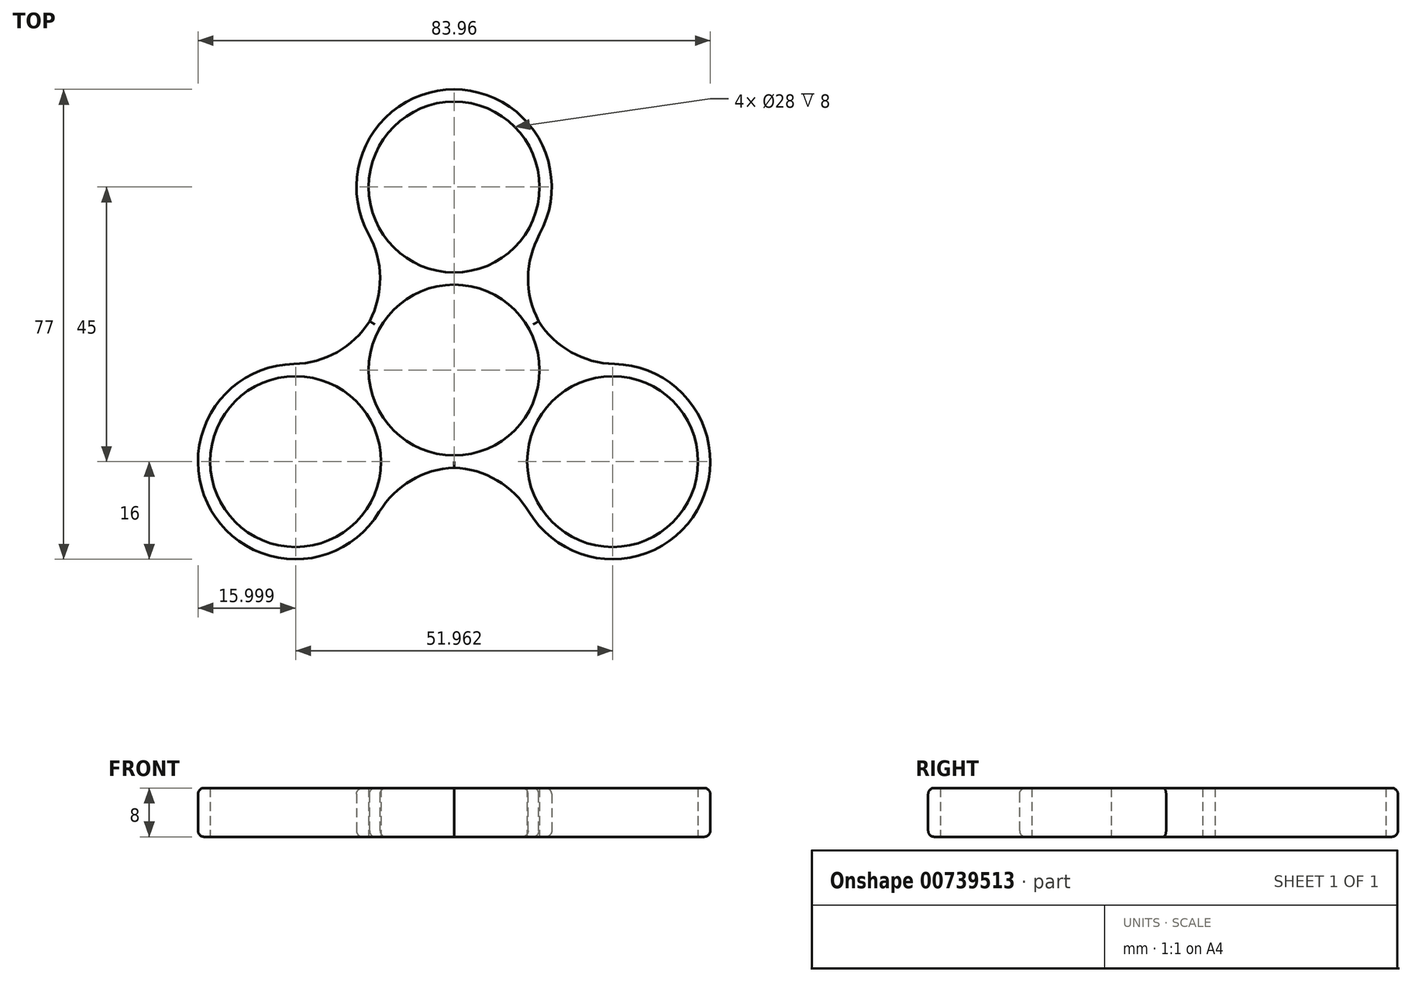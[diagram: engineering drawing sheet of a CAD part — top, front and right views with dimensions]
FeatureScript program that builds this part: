
annotation { "Feature Type Name" : "Feature", "Feature Type Description" : "" }
export const myFeature = defineFeature(function(context is Context, id is Id, definition is map)
    precondition{}
    {
        {
            var Q0;
            Q0=qCreatedBy(makeId("Top.planeOp"),FACE);
            var sketch = newSketch(context, id + "F0", { "sketchPlane" : qUnion([Q0])});
            skCircle(sketch, "E0", {"center": v(0, 0) * mm, "radius": 14 * mm});
            skCircle(sketch, "E1", {"center": v(25.98, -15) * mm, "radius": 14 * mm});
            skCircle(sketch, "E2", {"center": v(-25.98, -15) * mm, "radius": 14 * mm});
            skCircle(sketch, "E3", {"center": v(0, 30) * mm, "radius": 14 * mm});
            skCircle(sketch, "E4", {"center": v(0, 0) * mm, "radius": 30 * mm});
            skLineSegment(sketch, "E5", {"start": v(0, 0) * mm, "end": v(0, 45.5) * mm});
            skLineSegment(sketch, "E6", {"start": v(0, 0) * mm, "end": v(46, -26.56) * mm});
            skLineSegment(sketch, "E7", {"start": v(0, 0) * mm, "end": v(-45.6, -26.33) * mm});
            skCircle(sketch, "E8", {"center": v(0, 30) * mm, "radius": 16 * mm});
            skCircle(sketch, "E9", {"center": v(0, 0) * mm, "radius": 16 * mm});
            skCircle(sketch, "E10", {"center": v(-25.98, -15) * mm, "radius": 16 * mm});
            skCircle(sketch, "E11", {"center": v(25.98, -15) * mm, "radius": 16 * mm});
            skSolve(sketch);
        }
        {
            var Q0;
            {var subQ0=sQuery(id+"F0.wireOp",EDGE,"E4");var subQ1=sQuery(id+"F0.wireOp",EDGE,"E1");var subQ2=makeQuery(id+"F0.imprint","INTERSECT",VERTEX,{"disambiguationData":[OD(1.0)],"derivedFrom":[subQ1,subQ0]});Q0=makeQuery(id+"F0.imprint","IMPRINT",FACE,{"disambiguationData":[TD([[makeQuery(id+"F0.imprint","IMPRINT",EDGE,{"disambiguationData":[TD([[subQ2,-1.0]])],"derivedFrom":subQ1}),-1.0]])]});}
            var Q1;
            {var subQ0=sQuery(id+"F0.wireOp",EDGE,"E4");var subQ1=sQuery(id+"F0.wireOp",EDGE,"E1");var subQ2=makeQuery(id+"F0.imprint","INTERSECT",VERTEX,{"disambiguationData":[OD(0.0)],"derivedFrom":[subQ1,subQ0]});Q1=makeQuery(id+"F0.imprint","IMPRINT",FACE,{"disambiguationData":[TD([[makeQuery(id+"F0.imprint","IMPRINT",EDGE,{"disambiguationData":[TD([[subQ2,1.0]])],"derivedFrom":subQ1}),-1.0]])]});}
            var Q2;
            {var subQ0=sQuery(id+"F0.wireOp",EDGE,"E4");var subQ1=sQuery(id+"F0.wireOp",EDGE,"E2");var subQ2=makeQuery(id+"F0.imprint","INTERSECT",VERTEX,{"disambiguationData":[OD(0.0)],"derivedFrom":[subQ1,subQ0]});Q2=makeQuery(id+"F0.imprint","IMPRINT",FACE,{"disambiguationData":[TD([[makeQuery(id+"F0.imprint","IMPRINT",EDGE,{"disambiguationData":[TD([[subQ2,-1.0]])],"derivedFrom":subQ1}),-1.0]])]});}
            var Q3;
            {var subQ0=sQuery(id+"F0.wireOp",EDGE,"E7");var subQ1=sQuery(id+"F0.wireOp",EDGE,"E2");var subQ2=makeQuery(id+"F0.imprint","INTERSECT",VERTEX,{"derivedFrom":[subQ1,subQ0]});Q3=makeQuery(id+"F0.imprint","IMPRINT",FACE,{"disambiguationData":[TD([[makeQuery(id+"F0.imprint","IMPRINT",EDGE,{"disambiguationData":[TD([[subQ2,-1.0]])],"derivedFrom":subQ1}),-1.0]])]});}
            var Q4;
            {var subQ0=sQuery(id+"F0.wireOp",EDGE,"E4");var subQ5=sQuery(id+"F0.wireOp",EDGE,"E11");var subQ6=makeQuery(id+"F0.imprint","INTERSECT",VERTEX,{"disambiguationData":[OD(0.0)],"derivedFrom":[subQ0,subQ5]});Q4=makeQuery(id+"F0.imprint","IMPRINT",FACE,{"disambiguationData":[TD([[makeQuery(id+"F0.imprint","IMPRINT",EDGE,{"disambiguationData":[TD([[subQ6,1.0]])],"derivedFrom":subQ0}),1.0]])]});}
            var Q5;
            {var subQ0=sQuery(id+"F0.wireOp",EDGE,"E4");var subQ5=sQuery(id+"F0.wireOp",EDGE,"E11");var subQ6=makeQuery(id+"F0.imprint","INTERSECT",VERTEX,{"disambiguationData":[OD(1.0)],"derivedFrom":[subQ0,subQ5]});Q5=makeQuery(id+"F0.imprint","IMPRINT",FACE,{"disambiguationData":[TD([[makeQuery(id+"F0.imprint","IMPRINT",EDGE,{"disambiguationData":[TD([[subQ6,-1.0]])],"derivedFrom":subQ0}),1.0]])]});}
            var Q6;
            {var subQ0=sQuery(id+"F0.wireOp",EDGE,"E4");var subQ5=sQuery(id+"F0.wireOp",EDGE,"E10");var subQ7=makeQuery(id+"F0.imprint","INTERSECT",VERTEX,{"disambiguationData":[OD(0.0)],"derivedFrom":[subQ0,subQ5]});Q6=makeQuery(id+"F0.imprint","IMPRINT",FACE,{"disambiguationData":[TD([[makeQuery(id+"F0.imprint","IMPRINT",EDGE,{"disambiguationData":[TD([[subQ7,-1.0]])],"derivedFrom":subQ0}),1.0]])]});}
            var Q7;
            {var subQ0=sQuery(id+"F0.wireOp",EDGE,"E4");var subQ5=sQuery(id+"F0.wireOp",EDGE,"E10");var subQ6=makeQuery(id+"F0.imprint","INTERSECT",VERTEX,{"disambiguationData":[OD(1.0)],"derivedFrom":[subQ0,subQ5]});Q7=makeQuery(id+"F0.imprint","IMPRINT",FACE,{"disambiguationData":[TD([[makeQuery(id+"F0.imprint","IMPRINT",EDGE,{"disambiguationData":[TD([[subQ6,1.0]])],"derivedFrom":subQ0}),1.0]])]});}
            var Q8;
            {var subQ3=sQuery(id+"F0.wireOp",EDGE,"E3");var subQ5=makeQuery(id+"F0.imprint","INTERSECT",VERTEX,{"derivedFrom":[subQ3,sQuery(id+"F0.wireOp",EDGE,"E5")]});Q8=makeQuery(id+"F0.imprint","IMPRINT",FACE,{"disambiguationData":[TD([[makeQuery(id+"F0.imprint","IMPRINT",EDGE,{"disambiguationData":[TD([[subQ5,-1.0]])],"derivedFrom":subQ3}),-1.0]])]});}
            var Q9;
            {var subQ0=sQuery(id+"F0.wireOp",EDGE,"E4");var subQ5=sQuery(id+"F0.wireOp",EDGE,"E8");var subQ6=makeQuery(id+"F0.imprint","INTERSECT",VERTEX,{"disambiguationData":[OD(1.0)],"derivedFrom":[subQ0,subQ5]});Q9=makeQuery(id+"F0.imprint","IMPRINT",FACE,{"disambiguationData":[TD([[makeQuery(id+"F0.imprint","IMPRINT",EDGE,{"disambiguationData":[TD([[subQ6,1.0]])],"derivedFrom":subQ0}),1.0]])]});}
            var Q10;
            {var subQ0=sQuery(id+"F0.wireOp",EDGE,"E4");var subQ5=sQuery(id+"F0.wireOp",EDGE,"E8");var subQ6=makeQuery(id+"F0.imprint","INTERSECT",VERTEX,{"disambiguationData":[OD(0.0)],"derivedFrom":[subQ0,subQ5]});Q10=makeQuery(id+"F0.imprint","IMPRINT",FACE,{"disambiguationData":[TD([[makeQuery(id+"F0.imprint","IMPRINT",EDGE,{"disambiguationData":[TD([[subQ6,-1.0]])],"derivedFrom":subQ0}),1.0]])]});}
            var Q11;
            {var subQ0=sQuery(id+"F0.wireOp",EDGE,"E10");var subQ5=sQuery(id+"F0.wireOp",EDGE,"E9");var subQ7=makeQuery(id+"F0.imprint","INTERSECT",VERTEX,{"disambiguationData":[OD(1.0)],"derivedFrom":[subQ5,subQ0]});Q11=makeQuery(id+"F0.imprint","IMPRINT",FACE,{"disambiguationData":[TD([[makeQuery(id+"F0.imprint","IMPRINT",EDGE,{"disambiguationData":[TD([[subQ7,-1.0]])],"derivedFrom":subQ5}),1.0]])]});}
            var Q12;
            {var subQ3=sQuery(id+"F0.wireOp",EDGE,"E8");var subQ5=sQuery(id+"F0.wireOp",EDGE,"E9");var subQ6=makeQuery(id+"F0.imprint","INTERSECT",VERTEX,{"disambiguationData":[OD(0.0)],"derivedFrom":[subQ3,subQ5]});Q12=makeQuery(id+"F0.imprint","IMPRINT",FACE,{"disambiguationData":[TD([[makeQuery(id+"F0.imprint","IMPRINT",EDGE,{"disambiguationData":[TD([[subQ6,-1.0]])],"derivedFrom":subQ5}),1.0]])]});}
            var Q13;
            {var subQ0=sQuery(id+"F0.wireOp",EDGE,"E10");var subQ3=sQuery(id+"F0.wireOp",EDGE,"E9");var subQ5=makeQuery(id+"F0.imprint","INTERSECT",VERTEX,{"disambiguationData":[OD(0.0)],"derivedFrom":[subQ3,subQ0]});Q13=makeQuery(id+"F0.imprint","IMPRINT",FACE,{"disambiguationData":[TD([[makeQuery(id+"F0.imprint","IMPRINT",EDGE,{"disambiguationData":[TD([[subQ5,-1.0]])],"derivedFrom":subQ3}),1.0]])]});}
            var Q14;
            {var subQ0=sQuery(id+"F0.wireOp",EDGE,"E10");var subQ3=sQuery(id+"F0.wireOp",EDGE,"E9");var subQ5=makeQuery(id+"F0.imprint","INTERSECT",VERTEX,{"disambiguationData":[OD(1.0)],"derivedFrom":[subQ3,subQ0]});Q14=makeQuery(id+"F0.imprint","IMPRINT",FACE,{"disambiguationData":[TD([[makeQuery(id+"F0.imprint","IMPRINT",EDGE,{"disambiguationData":[TD([[subQ5,1.0]])],"derivedFrom":subQ3}),1.0]])]});}
            var Q15;
            {var subQ0=sQuery(id+"F0.wireOp",EDGE,"E11");var subQ3=sQuery(id+"F0.wireOp",EDGE,"E9");var subQ5=makeQuery(id+"F0.imprint","INTERSECT",VERTEX,{"disambiguationData":[OD(0.0)],"derivedFrom":[subQ3,subQ0]});Q15=makeQuery(id+"F0.imprint","IMPRINT",FACE,{"disambiguationData":[TD([[makeQuery(id+"F0.imprint","IMPRINT",EDGE,{"disambiguationData":[TD([[subQ5,-1.0]])],"derivedFrom":subQ3}),1.0]])]});}
            var Q16;
            {var subQ0=sQuery(id+"F0.wireOp",EDGE,"E11");var subQ3=sQuery(id+"F0.wireOp",EDGE,"E9");var subQ5=makeQuery(id+"F0.imprint","INTERSECT",VERTEX,{"disambiguationData":[OD(1.0)],"derivedFrom":[subQ3,subQ0]});Q16=makeQuery(id+"F0.imprint","IMPRINT",FACE,{"disambiguationData":[TD([[makeQuery(id+"F0.imprint","IMPRINT",EDGE,{"disambiguationData":[TD([[subQ5,1.0]])],"derivedFrom":subQ3}),1.0]])]});}
            var Q17;
            {var subQ0=sQuery(id+"F0.wireOp",EDGE,"E8");var subQ5=sQuery(id+"F0.wireOp",EDGE,"E9");var subQ6=makeQuery(id+"F0.imprint","INTERSECT",VERTEX,{"disambiguationData":[OD(1.0)],"derivedFrom":[subQ0,subQ5]});Q17=makeQuery(id+"F0.imprint","IMPRINT",FACE,{"disambiguationData":[TD([[makeQuery(id+"F0.imprint","IMPRINT",EDGE,{"disambiguationData":[TD([[subQ6,1.0]])],"derivedFrom":subQ5}),1.0]])]});}
            var Q18;
            {var subQ0=sQuery(id+"F0.wireOp",EDGE,"E8");var subQ3=sQuery(id+"F0.wireOp",EDGE,"E9");var subQ5=makeQuery(id+"F0.imprint","INTERSECT",VERTEX,{"disambiguationData":[OD(1.0)],"derivedFrom":[subQ0,subQ3]});Q18=makeQuery(id+"F0.imprint","IMPRINT",FACE,{"disambiguationData":[TD([[makeQuery(id+"F0.imprint","IMPRINT",EDGE,{"disambiguationData":[TD([[subQ5,1.0]])],"derivedFrom":subQ0}),1.0]])]});}
            var Q19;
            {var subQ0=sQuery(id+"F0.wireOp",EDGE,"E8");var subQ3=sQuery(id+"F0.wireOp",EDGE,"E9");var subQ5=makeQuery(id+"F0.imprint","INTERSECT",VERTEX,{"disambiguationData":[OD(0.0)],"derivedFrom":[subQ0,subQ3]});Q19=makeQuery(id+"F0.imprint","IMPRINT",FACE,{"disambiguationData":[TD([[makeQuery(id+"F0.imprint","IMPRINT",EDGE,{"disambiguationData":[TD([[subQ5,-1.0]])],"derivedFrom":subQ0}),1.0]])]});}
            extrude(context, id + "F1", {"entities" : qUnion([Q0, Q1, Q2, Q3, Q4, Q5, Q6, Q7, Q8, Q9, Q10, Q11, Q12, Q13, Q14, Q15, Q16, Q17, Q18, Q19]), "depth" : 8 * mm, "offsetDistance" : 25 * mm});
        }
        {
            var Q0;
            {var subQ0=sQuery(id+"F0.wireOp",EDGE,"E10");var subQ1=sQuery(id+"F0.wireOp",EDGE,"E9");Q0=makeQuery(id+"F1.opExtrude","SWEPT_EDGE",EDGE,{"disambiguationData":[OSD([subQ1,subQ0]),TDD([makeQuery(id+"F0.imprint","INTERSECT",VERTEX,{"disambiguationData":[OD(1.0)],"derivedFrom":[subQ1,subQ0]})])]});}
            var Q1;
            {var subQ0=sQuery(id+"F0.wireOp",EDGE,"E11");var subQ1=sQuery(id+"F0.wireOp",EDGE,"E9");Q1=makeQuery(id+"F1.opExtrude","SWEPT_EDGE",EDGE,{"disambiguationData":[OSD([subQ1,subQ0]),TDD([makeQuery(id+"F0.imprint","INTERSECT",VERTEX,{"disambiguationData":[OD(0.0)],"derivedFrom":[subQ1,subQ0]})])]});}
            var Q2;
            {var subQ0=sQuery(id+"F0.wireOp",EDGE,"E11");var subQ1=sQuery(id+"F0.wireOp",EDGE,"E9");Q2=makeQuery(id+"F1.opExtrude","SWEPT_EDGE",EDGE,{"disambiguationData":[OSD([subQ1,subQ0]),TDD([makeQuery(id+"F0.imprint","INTERSECT",VERTEX,{"disambiguationData":[OD(1.0)],"derivedFrom":[subQ1,subQ0]})])]});}
            var Q3;
            {var subQ0=sQuery(id+"F0.wireOp",EDGE,"E9");var subQ1=sQuery(id+"F0.wireOp",EDGE,"E8");Q3=makeQuery(id+"F1.opExtrude","SWEPT_EDGE",EDGE,{"disambiguationData":[OSD([subQ1,subQ0]),TDD([makeQuery(id+"F0.imprint","INTERSECT",VERTEX,{"disambiguationData":[OD(1.0)],"derivedFrom":[subQ1,subQ0]})])]});}
            var Q4;
            {var subQ0=sQuery(id+"F0.wireOp",EDGE,"E9");var subQ1=sQuery(id+"F0.wireOp",EDGE,"E8");Q4=makeQuery(id+"F1.opExtrude","SWEPT_EDGE",EDGE,{"disambiguationData":[OSD([subQ1,subQ0]),TDD([makeQuery(id+"F0.imprint","INTERSECT",VERTEX,{"disambiguationData":[OD(0.0)],"derivedFrom":[subQ1,subQ0]})])]});}
            var Q5;
            {var subQ0=sQuery(id+"F0.wireOp",EDGE,"E10");var subQ1=sQuery(id+"F0.wireOp",EDGE,"E9");Q5=makeQuery(id+"F1.opExtrude","SWEPT_EDGE",EDGE,{"disambiguationData":[OSD([subQ1,subQ0]),TDD([makeQuery(id+"F0.imprint","INTERSECT",VERTEX,{"disambiguationData":[OD(0.0)],"derivedFrom":[subQ1,subQ0]})])]});}
            fillet(context, id + "F2", {"entities" : qUnion([Q0, Q1, Q2, Q3, Q4, Q5]), "radius" : 15 * mm, "tangentPropagation" : true, "allowEdgeOverflow" : false});
        }
        {
            var Q0;
            Q0=makeQuery(id+"F1.opExtrude","CAP_EDGE",EDGE,{"disambiguationData":[OSD([sQuery(id+"F0.wireOp",EDGE,"E10")])],"isStart":false});
            var Q1;
            {var subQ0=sQuery(id+"F0.wireOp",EDGE,"E10");var subQ1=sQuery(id+"F0.wireOp",EDGE,"E9");Q1=makeQuery(id+"F2.opFillet","BLEND_EDGE",EDGE,{"blendedFrom":[makeQuery(id+"F1.opExtrude","SWEPT_EDGE",EDGE,{"disambiguationData":[OSD([subQ1,subQ0]),TDD([makeQuery(id+"F0.imprint","INTERSECT",VERTEX,{"disambiguationData":[OD(1.0)],"derivedFrom":[subQ1,subQ0]})])]}),makeQuery(id+"F1.opExtrude","CAP_FACE",FACE,{"disambiguationData":[OSD([sQuery(id+"F0.wireOp",EDGE,"E0"),sQuery(id+"F0.wireOp",EDGE,"E1"),sQuery(id+"F0.wireOp",EDGE,"E2"),sQuery(id+"F0.wireOp",EDGE,"E3"),sQuery(id+"F0.wireOp",EDGE,"E8"),subQ1,subQ0,sQuery(id+"F0.wireOp",EDGE,"E11")])],"isStart":false})],"blendedInto":[makeQuery(id+"F1.opExtrude","CAP_FACE",FACE,{"disambiguationData":[OSD([sQuery(id+"F0.wireOp",EDGE,"E0"),sQuery(id+"F0.wireOp",EDGE,"E1"),sQuery(id+"F0.wireOp",EDGE,"E2"),sQuery(id+"F0.wireOp",EDGE,"E3"),sQuery(id+"F0.wireOp",EDGE,"E8"),subQ1,subQ0,sQuery(id+"F0.wireOp",EDGE,"E11")])],"isStart":false})]});}
            var Q2;
            {var subQ0=sQuery(id+"F0.wireOp",EDGE,"E11");var subQ1=sQuery(id+"F0.wireOp",EDGE,"E9");Q2=makeQuery(id+"F2.opFillet","BLEND_EDGE",EDGE,{"blendedFrom":[makeQuery(id+"F1.opExtrude","SWEPT_EDGE",EDGE,{"disambiguationData":[OSD([subQ1,subQ0]),TDD([makeQuery(id+"F0.imprint","INTERSECT",VERTEX,{"disambiguationData":[OD(0.0)],"derivedFrom":[subQ1,subQ0]})])]}),makeQuery(id+"F1.opExtrude","CAP_FACE",FACE,{"disambiguationData":[OSD([sQuery(id+"F0.wireOp",EDGE,"E0"),sQuery(id+"F0.wireOp",EDGE,"E1"),sQuery(id+"F0.wireOp",EDGE,"E2"),sQuery(id+"F0.wireOp",EDGE,"E3"),sQuery(id+"F0.wireOp",EDGE,"E8"),subQ1,sQuery(id+"F0.wireOp",EDGE,"E10"),subQ0])],"isStart":false})],"blendedInto":[makeQuery(id+"F1.opExtrude","CAP_FACE",FACE,{"disambiguationData":[OSD([sQuery(id+"F0.wireOp",EDGE,"E0"),sQuery(id+"F0.wireOp",EDGE,"E1"),sQuery(id+"F0.wireOp",EDGE,"E2"),sQuery(id+"F0.wireOp",EDGE,"E3"),sQuery(id+"F0.wireOp",EDGE,"E8"),subQ1,sQuery(id+"F0.wireOp",EDGE,"E10"),subQ0])],"isStart":false})]});}
            var Q3;
            Q3=makeQuery(id+"F1.opExtrude","CAP_EDGE",EDGE,{"disambiguationData":[OSD([sQuery(id+"F0.wireOp",EDGE,"E11")])],"isStart":false});
            var Q4;
            {var subQ0=sQuery(id+"F0.wireOp",EDGE,"E11");var subQ1=sQuery(id+"F0.wireOp",EDGE,"E9");Q4=makeQuery(id+"F2.opFillet","BLEND_EDGE",EDGE,{"blendedFrom":[makeQuery(id+"F1.opExtrude","SWEPT_EDGE",EDGE,{"disambiguationData":[OSD([subQ1,subQ0]),TDD([makeQuery(id+"F0.imprint","INTERSECT",VERTEX,{"disambiguationData":[OD(1.0)],"derivedFrom":[subQ1,subQ0]})])]}),makeQuery(id+"F1.opExtrude","CAP_FACE",FACE,{"disambiguationData":[OSD([sQuery(id+"F0.wireOp",EDGE,"E0"),sQuery(id+"F0.wireOp",EDGE,"E1"),sQuery(id+"F0.wireOp",EDGE,"E2"),sQuery(id+"F0.wireOp",EDGE,"E3"),sQuery(id+"F0.wireOp",EDGE,"E8"),subQ1,sQuery(id+"F0.wireOp",EDGE,"E10"),subQ0])],"isStart":false})],"blendedInto":[makeQuery(id+"F1.opExtrude","CAP_FACE",FACE,{"disambiguationData":[OSD([sQuery(id+"F0.wireOp",EDGE,"E0"),sQuery(id+"F0.wireOp",EDGE,"E1"),sQuery(id+"F0.wireOp",EDGE,"E2"),sQuery(id+"F0.wireOp",EDGE,"E3"),sQuery(id+"F0.wireOp",EDGE,"E8"),subQ1,sQuery(id+"F0.wireOp",EDGE,"E10"),subQ0])],"isStart":false})]});}
            var Q5;
            {var subQ0=sQuery(id+"F0.wireOp",EDGE,"E9");var subQ1=sQuery(id+"F0.wireOp",EDGE,"E8");Q5=makeQuery(id+"F2.opFillet","BLEND_EDGE",EDGE,{"blendedFrom":[makeQuery(id+"F1.opExtrude","SWEPT_EDGE",EDGE,{"disambiguationData":[OSD([subQ1,subQ0]),TDD([makeQuery(id+"F0.imprint","INTERSECT",VERTEX,{"disambiguationData":[OD(1.0)],"derivedFrom":[subQ1,subQ0]})])]}),makeQuery(id+"F1.opExtrude","CAP_FACE",FACE,{"disambiguationData":[OSD([sQuery(id+"F0.wireOp",EDGE,"E0"),sQuery(id+"F0.wireOp",EDGE,"E1"),sQuery(id+"F0.wireOp",EDGE,"E2"),sQuery(id+"F0.wireOp",EDGE,"E3"),subQ1,subQ0,sQuery(id+"F0.wireOp",EDGE,"E10"),sQuery(id+"F0.wireOp",EDGE,"E11")])],"isStart":false})],"blendedInto":[makeQuery(id+"F1.opExtrude","CAP_FACE",FACE,{"disambiguationData":[OSD([sQuery(id+"F0.wireOp",EDGE,"E0"),sQuery(id+"F0.wireOp",EDGE,"E1"),sQuery(id+"F0.wireOp",EDGE,"E2"),sQuery(id+"F0.wireOp",EDGE,"E3"),subQ1,subQ0,sQuery(id+"F0.wireOp",EDGE,"E10"),sQuery(id+"F0.wireOp",EDGE,"E11")])],"isStart":false})]});}
            var Q6;
            Q6=makeQuery(id+"F1.opExtrude","CAP_EDGE",EDGE,{"disambiguationData":[OSD([sQuery(id+"F0.wireOp",EDGE,"E8")])],"isStart":false});
            var Q7;
            {var subQ0=sQuery(id+"F0.wireOp",EDGE,"E9");var subQ1=sQuery(id+"F0.wireOp",EDGE,"E8");Q7=makeQuery(id+"F2.opFillet","BLEND_EDGE",EDGE,{"blendedFrom":[makeQuery(id+"F1.opExtrude","SWEPT_EDGE",EDGE,{"disambiguationData":[OSD([subQ1,subQ0]),TDD([makeQuery(id+"F0.imprint","INTERSECT",VERTEX,{"disambiguationData":[OD(0.0)],"derivedFrom":[subQ1,subQ0]})])]}),makeQuery(id+"F1.opExtrude","CAP_FACE",FACE,{"disambiguationData":[OSD([sQuery(id+"F0.wireOp",EDGE,"E0"),sQuery(id+"F0.wireOp",EDGE,"E1"),sQuery(id+"F0.wireOp",EDGE,"E2"),sQuery(id+"F0.wireOp",EDGE,"E3"),subQ1,subQ0,sQuery(id+"F0.wireOp",EDGE,"E10"),sQuery(id+"F0.wireOp",EDGE,"E11")])],"isStart":false})],"blendedInto":[makeQuery(id+"F1.opExtrude","CAP_FACE",FACE,{"disambiguationData":[OSD([sQuery(id+"F0.wireOp",EDGE,"E0"),sQuery(id+"F0.wireOp",EDGE,"E1"),sQuery(id+"F0.wireOp",EDGE,"E2"),sQuery(id+"F0.wireOp",EDGE,"E3"),subQ1,subQ0,sQuery(id+"F0.wireOp",EDGE,"E10"),sQuery(id+"F0.wireOp",EDGE,"E11")])],"isStart":false})]});}
            var Q8;
            {var subQ0=sQuery(id+"F0.wireOp",EDGE,"E10");var subQ1=sQuery(id+"F0.wireOp",EDGE,"E9");Q8=makeQuery(id+"F2.opFillet","BLEND_EDGE",EDGE,{"blendedFrom":[makeQuery(id+"F1.opExtrude","SWEPT_EDGE",EDGE,{"disambiguationData":[OSD([subQ1,subQ0]),TDD([makeQuery(id+"F0.imprint","INTERSECT",VERTEX,{"disambiguationData":[OD(0.0)],"derivedFrom":[subQ1,subQ0]})])]}),makeQuery(id+"F1.opExtrude","CAP_FACE",FACE,{"disambiguationData":[OSD([sQuery(id+"F0.wireOp",EDGE,"E0"),sQuery(id+"F0.wireOp",EDGE,"E1"),sQuery(id+"F0.wireOp",EDGE,"E2"),sQuery(id+"F0.wireOp",EDGE,"E3"),sQuery(id+"F0.wireOp",EDGE,"E8"),subQ1,subQ0,sQuery(id+"F0.wireOp",EDGE,"E11")])],"isStart":false})],"blendedInto":[makeQuery(id+"F1.opExtrude","CAP_FACE",FACE,{"disambiguationData":[OSD([sQuery(id+"F0.wireOp",EDGE,"E0"),sQuery(id+"F0.wireOp",EDGE,"E1"),sQuery(id+"F0.wireOp",EDGE,"E2"),sQuery(id+"F0.wireOp",EDGE,"E3"),sQuery(id+"F0.wireOp",EDGE,"E8"),subQ1,subQ0,sQuery(id+"F0.wireOp",EDGE,"E11")])],"isStart":false})]});}
            fillet(context, id + "F3", {"entities" : qUnion([Q0, Q1, Q2, Q3, Q4, Q5, Q6, Q7, Q8]), "radius" : 1 * mm, "tangentPropagation" : true, "allowEdgeOverflow" : false});
        }
        {
            var Q0;
            Q0=makeQuery(id+"F1.opExtrude","CAP_EDGE",EDGE,{"disambiguationData":[OSD([sQuery(id+"F0.wireOp",EDGE,"E11")])],"isStart":true});
            var Q1;
            {var subQ0=sQuery(id+"F0.wireOp",EDGE,"E11");var subQ1=sQuery(id+"F0.wireOp",EDGE,"E9");Q1=makeQuery(id+"F2.opFillet","BLEND_EDGE",EDGE,{"blendedFrom":[makeQuery(id+"F1.opExtrude","SWEPT_EDGE",EDGE,{"disambiguationData":[OSD([subQ1,subQ0]),TDD([makeQuery(id+"F0.imprint","INTERSECT",VERTEX,{"disambiguationData":[OD(0.0)],"derivedFrom":[subQ1,subQ0]})])]}),makeQuery(id+"F1.opExtrude","CAP_FACE",FACE,{"disambiguationData":[OSD([sQuery(id+"F0.wireOp",EDGE,"E0"),sQuery(id+"F0.wireOp",EDGE,"E1"),sQuery(id+"F0.wireOp",EDGE,"E2"),sQuery(id+"F0.wireOp",EDGE,"E3"),sQuery(id+"F0.wireOp",EDGE,"E8"),subQ1,sQuery(id+"F0.wireOp",EDGE,"E10"),subQ0])],"isStart":true})],"blendedInto":[makeQuery(id+"F1.opExtrude","CAP_FACE",FACE,{"disambiguationData":[OSD([sQuery(id+"F0.wireOp",EDGE,"E0"),sQuery(id+"F0.wireOp",EDGE,"E1"),sQuery(id+"F0.wireOp",EDGE,"E2"),sQuery(id+"F0.wireOp",EDGE,"E3"),sQuery(id+"F0.wireOp",EDGE,"E8"),subQ1,sQuery(id+"F0.wireOp",EDGE,"E10"),subQ0])],"isStart":true})]});}
            var Q2;
            {var subQ0=sQuery(id+"F0.wireOp",EDGE,"E10");var subQ1=sQuery(id+"F0.wireOp",EDGE,"E9");Q2=makeQuery(id+"F2.opFillet","BLEND_EDGE",EDGE,{"blendedFrom":[makeQuery(id+"F1.opExtrude","SWEPT_EDGE",EDGE,{"disambiguationData":[OSD([subQ1,subQ0]),TDD([makeQuery(id+"F0.imprint","INTERSECT",VERTEX,{"disambiguationData":[OD(1.0)],"derivedFrom":[subQ1,subQ0]})])]}),makeQuery(id+"F1.opExtrude","CAP_FACE",FACE,{"disambiguationData":[OSD([sQuery(id+"F0.wireOp",EDGE,"E0"),sQuery(id+"F0.wireOp",EDGE,"E1"),sQuery(id+"F0.wireOp",EDGE,"E2"),sQuery(id+"F0.wireOp",EDGE,"E3"),sQuery(id+"F0.wireOp",EDGE,"E8"),subQ1,subQ0,sQuery(id+"F0.wireOp",EDGE,"E11")])],"isStart":true})],"blendedInto":[makeQuery(id+"F1.opExtrude","CAP_FACE",FACE,{"disambiguationData":[OSD([sQuery(id+"F0.wireOp",EDGE,"E0"),sQuery(id+"F0.wireOp",EDGE,"E1"),sQuery(id+"F0.wireOp",EDGE,"E2"),sQuery(id+"F0.wireOp",EDGE,"E3"),sQuery(id+"F0.wireOp",EDGE,"E8"),subQ1,subQ0,sQuery(id+"F0.wireOp",EDGE,"E11")])],"isStart":true})]});}
            var Q3;
            Q3=makeQuery(id+"F1.opExtrude","CAP_EDGE",EDGE,{"disambiguationData":[OSD([sQuery(id+"F0.wireOp",EDGE,"E10")])],"isStart":true});
            var Q4;
            {var subQ0=sQuery(id+"F0.wireOp",EDGE,"E10");var subQ1=sQuery(id+"F0.wireOp",EDGE,"E9");Q4=makeQuery(id+"F2.opFillet","BLEND_EDGE",EDGE,{"blendedFrom":[makeQuery(id+"F1.opExtrude","SWEPT_EDGE",EDGE,{"disambiguationData":[OSD([subQ1,subQ0]),TDD([makeQuery(id+"F0.imprint","INTERSECT",VERTEX,{"disambiguationData":[OD(0.0)],"derivedFrom":[subQ1,subQ0]})])]}),makeQuery(id+"F1.opExtrude","CAP_FACE",FACE,{"disambiguationData":[OSD([sQuery(id+"F0.wireOp",EDGE,"E0"),sQuery(id+"F0.wireOp",EDGE,"E1"),sQuery(id+"F0.wireOp",EDGE,"E2"),sQuery(id+"F0.wireOp",EDGE,"E3"),sQuery(id+"F0.wireOp",EDGE,"E8"),subQ1,subQ0,sQuery(id+"F0.wireOp",EDGE,"E11")])],"isStart":true})],"blendedInto":[makeQuery(id+"F1.opExtrude","CAP_FACE",FACE,{"disambiguationData":[OSD([sQuery(id+"F0.wireOp",EDGE,"E0"),sQuery(id+"F0.wireOp",EDGE,"E1"),sQuery(id+"F0.wireOp",EDGE,"E2"),sQuery(id+"F0.wireOp",EDGE,"E3"),sQuery(id+"F0.wireOp",EDGE,"E8"),subQ1,subQ0,sQuery(id+"F0.wireOp",EDGE,"E11")])],"isStart":true})]});}
            var Q5;
            {var subQ0=sQuery(id+"F0.wireOp",EDGE,"E9");var subQ1=sQuery(id+"F0.wireOp",EDGE,"E8");Q5=makeQuery(id+"F2.opFillet","BLEND_EDGE",EDGE,{"blendedFrom":[makeQuery(id+"F1.opExtrude","SWEPT_EDGE",EDGE,{"disambiguationData":[OSD([subQ1,subQ0]),TDD([makeQuery(id+"F0.imprint","INTERSECT",VERTEX,{"disambiguationData":[OD(0.0)],"derivedFrom":[subQ1,subQ0]})])]}),makeQuery(id+"F1.opExtrude","CAP_FACE",FACE,{"disambiguationData":[OSD([sQuery(id+"F0.wireOp",EDGE,"E0"),sQuery(id+"F0.wireOp",EDGE,"E1"),sQuery(id+"F0.wireOp",EDGE,"E2"),sQuery(id+"F0.wireOp",EDGE,"E3"),subQ1,subQ0,sQuery(id+"F0.wireOp",EDGE,"E10"),sQuery(id+"F0.wireOp",EDGE,"E11")])],"isStart":true})],"blendedInto":[makeQuery(id+"F1.opExtrude","CAP_FACE",FACE,{"disambiguationData":[OSD([sQuery(id+"F0.wireOp",EDGE,"E0"),sQuery(id+"F0.wireOp",EDGE,"E1"),sQuery(id+"F0.wireOp",EDGE,"E2"),sQuery(id+"F0.wireOp",EDGE,"E3"),subQ1,subQ0,sQuery(id+"F0.wireOp",EDGE,"E10"),sQuery(id+"F0.wireOp",EDGE,"E11")])],"isStart":true})]});}
            var Q6;
            Q6=makeQuery(id+"F1.opExtrude","CAP_EDGE",EDGE,{"disambiguationData":[OSD([sQuery(id+"F0.wireOp",EDGE,"E8")])],"isStart":true});
            var Q7;
            {var subQ0=sQuery(id+"F0.wireOp",EDGE,"E9");var subQ1=sQuery(id+"F0.wireOp",EDGE,"E8");Q7=makeQuery(id+"F2.opFillet","BLEND_EDGE",EDGE,{"blendedFrom":[makeQuery(id+"F1.opExtrude","SWEPT_EDGE",EDGE,{"disambiguationData":[OSD([subQ1,subQ0]),TDD([makeQuery(id+"F0.imprint","INTERSECT",VERTEX,{"disambiguationData":[OD(1.0)],"derivedFrom":[subQ1,subQ0]})])]}),makeQuery(id+"F1.opExtrude","CAP_FACE",FACE,{"disambiguationData":[OSD([sQuery(id+"F0.wireOp",EDGE,"E0"),sQuery(id+"F0.wireOp",EDGE,"E1"),sQuery(id+"F0.wireOp",EDGE,"E2"),sQuery(id+"F0.wireOp",EDGE,"E3"),subQ1,subQ0,sQuery(id+"F0.wireOp",EDGE,"E10"),sQuery(id+"F0.wireOp",EDGE,"E11")])],"isStart":true})],"blendedInto":[makeQuery(id+"F1.opExtrude","CAP_FACE",FACE,{"disambiguationData":[OSD([sQuery(id+"F0.wireOp",EDGE,"E0"),sQuery(id+"F0.wireOp",EDGE,"E1"),sQuery(id+"F0.wireOp",EDGE,"E2"),sQuery(id+"F0.wireOp",EDGE,"E3"),subQ1,subQ0,sQuery(id+"F0.wireOp",EDGE,"E10"),sQuery(id+"F0.wireOp",EDGE,"E11")])],"isStart":true})]});}
            var Q8;
            {var subQ0=sQuery(id+"F0.wireOp",EDGE,"E11");var subQ1=sQuery(id+"F0.wireOp",EDGE,"E9");Q8=makeQuery(id+"F2.opFillet","BLEND_EDGE",EDGE,{"blendedFrom":[makeQuery(id+"F1.opExtrude","SWEPT_EDGE",EDGE,{"disambiguationData":[OSD([subQ1,subQ0]),TDD([makeQuery(id+"F0.imprint","INTERSECT",VERTEX,{"disambiguationData":[OD(1.0)],"derivedFrom":[subQ1,subQ0]})])]}),makeQuery(id+"F1.opExtrude","CAP_FACE",FACE,{"disambiguationData":[OSD([sQuery(id+"F0.wireOp",EDGE,"E0"),sQuery(id+"F0.wireOp",EDGE,"E1"),sQuery(id+"F0.wireOp",EDGE,"E2"),sQuery(id+"F0.wireOp",EDGE,"E3"),sQuery(id+"F0.wireOp",EDGE,"E8"),subQ1,sQuery(id+"F0.wireOp",EDGE,"E10"),subQ0])],"isStart":true})],"blendedInto":[makeQuery(id+"F1.opExtrude","CAP_FACE",FACE,{"disambiguationData":[OSD([sQuery(id+"F0.wireOp",EDGE,"E0"),sQuery(id+"F0.wireOp",EDGE,"E1"),sQuery(id+"F0.wireOp",EDGE,"E2"),sQuery(id+"F0.wireOp",EDGE,"E3"),sQuery(id+"F0.wireOp",EDGE,"E8"),subQ1,sQuery(id+"F0.wireOp",EDGE,"E10"),subQ0])],"isStart":true})]});}
            fillet(context, id + "F4", {"entities" : qUnion([Q0, Q1, Q2, Q3, Q4, Q5, Q6, Q7, Q8]), "radius" : 1 * mm, "tangentPropagation" : true, "allowEdgeOverflow" : false});
        }
    });
